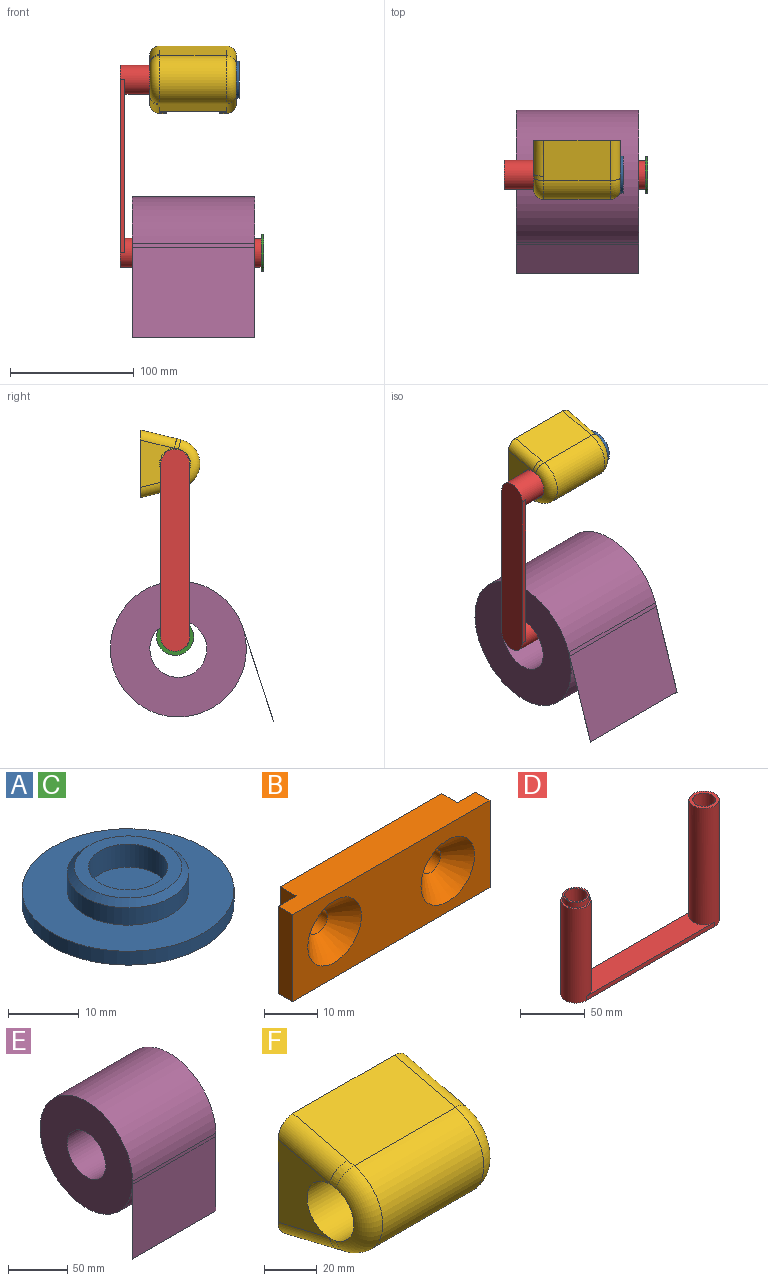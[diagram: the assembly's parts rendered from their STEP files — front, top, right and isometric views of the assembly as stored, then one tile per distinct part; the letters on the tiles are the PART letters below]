
ASSEMBLY  parts=6 mates=5
PART A: 8 faces, bbox 30x30x6.4 mm
  f0: cylinder r=15mm len=30mm, axis (0,0,-1), area 226.2mm2, adj f1,f2
  f1: plane 30x30mm, normal (0,0,1), area 474.5mm2, adj f0,f4
  f2: plane 30x30mm, normal (0,0,-1), area 706.9mm2, adj f0
  f3: cylinder r=5.6mm len=11.2mm, axis (0,0,-1), area 140.7mm2, adj f5,f6
  f4: cylinder r=8.6mm len=17.2mm, axis (0,0,-1), area 162.1mm2, adj f1,f7
  f5: plane 15.2x15.2mm, normal (0,0,1), area 82.9mm2, adj f3,f7
  f6: plane 11.2x11.2mm, normal (0,0,1), area 98.5mm2, adj f3
  f7: cone r=7.6mm half-angle=45deg, axis (0,0,-1), area 72mm2, adj f4,f5
PART B: 14 faces, bbox 52.4x8x20 mm
  f0: plane 42.8x20mm, normal (0,1,0), area 813.5mm2, adj f1,f7,f8,f9,f10,f11
  f1: plane 20x4.2mm, normal (-1,0,0), area 84mm2, adj f0,f2,f8,f9
  f2: plane 20x4.8mm, normal (0,1,0), area 96mm2, adj f1,f3,f8,f9
  f3: plane 20x3.8mm, normal (-1,0,0), area 76mm2, adj f2,f4,f8,f9
  f4: plane 52.4x20mm, normal (0,-1,0), area 731.3mm2, adj f3,f5,f8,f9,f12,f13
  f5: plane 20x3.8mm, normal (1,0,0), area 76mm2, adj f4,f6,f8,f9
  f6: plane 20x4.8mm, normal (0,1,0), area 96mm2, adj f5,f7,f8,f9
  f7: plane 20x4.2mm, normal (1,0,0), area 84mm2, adj f0,f6,f8,f9
  f8: plane 52.4x8mm, normal (0,0,1), area 378.9mm2, adj f0,f1,f2,f3,f4,f5,f6,f7
  f9: plane 52.4x8mm, normal (0,0,-1), area 378.9mm2, adj f0,f1,f2,f3,f4,f5,f6,f7
  f10: cylinder r=2.6mm len=5.2mm, axis (0,-1,0), area 57.2mm2, adj f0,f12
  f11: cylinder r=2.6mm len=5.2mm, axis (0,-1,0), area 57.2mm2, adj f0,f13
  f12: cone r=2.6mm half-angle=45deg, axis (0,-1,0), area 193.9mm2, adj f4,f10
  f13: cone r=2.6mm half-angle=45deg, axis (0,-1,0), area 193.9mm2, adj f4,f11
PART C: same geometry as A
PART D: 14 faces, bbox 163.4x23.4x114 mm
  f0: cylinder r=11.7mm len=88.9mm, axis (0,0,-1), area 6388.3mm2, adj f1,f3,f4,f5,f10
  f1: plane 140x4mm, normal (0,-1,0), area 560mm2, adj f0,f2,f4,f5
  f2: cylinder r=11.7mm len=114mm, axis (0,0,-1), area 8233.5mm2, adj f1,f3,f4,f5,f7
  f3: plane 140x4mm, normal (0,1,0), area 560mm2, adj f0,f2,f4,f5
  f4: plane 140x23.4mm, normal (0,0,1), area 2845.9mm2, adj f0,f1,f2,f3
  f5: plane 163.4x23.4mm, normal (0,0,-1), area 3706.1mm2, adj f0,f1,f2,f3
  f6: cylinder r=8.7mm len=110mm, axis (0,0,-1), area 6013mm2, adj f7,f8
  f7: plane 23.4x23.4mm, normal (0,0,1), area 192.3mm2, adj f2,f6
  f8: plane 17.4x17.4mm, normal (0,0,1), area 237.8mm2, adj f6
  f9: cylinder r=10.2mm len=20.4mm, axis (0,0,1), area 326.9mm2, adj f10,f13
  f10: plane 23.4x23.4mm, normal (0,0,1), area 103.2mm2, adj f0,f9
  f11: plane 17.4x17.4mm, normal (0,0,1), area 237.8mm2, adj f12
  f12: cylinder r=8.7mm len=90mm, axis (0,0,-1), area 4919.7mm2, adj f11,f13
  f13: plane 20.4x20.4mm, normal (0,0,1), area 89.1mm2, adj f9,f12
PART E: 7 faces, bbox 99x110x135 mm
  f0: cylinder r=55mm len=110mm, axis (-1,0,0), area 33883.5mm2, adj f2,f3,f4,f6
  f1: cylinder r=23mm len=99mm, axis (-1,0,0), area 14306.8mm2, adj f2,f3
  f2: plane 135x110mm, normal (1,0,0), area 7849.2mm2, adj f0,f1,f4,f5,f6
  f3: plane 135x110mm, normal (-1,0,0), area 7849.2mm2, adj f0,f1,f4,f5,f6
  f4: plane 99x76.69mm, normal (0,1,0), area 7591.8mm2, adj f0,f2,f3,f5
  f5: plane 99x0.1mm, normal (0,0,-1), area 9.9mm2, adj f2,f3,f4,f6
  f6: plane 99x80mm, normal (0,-1,0), area 7920mm2, adj f0,f2,f3,f5
PART F: 25 faces, bbox 70.4x51.5x54.6 mm
  f0: plane 54.02x32.67mm, normal (0,-0.23,-0.97), area 1408.5mm2, adj f3,f4,f12,f13,f16,f17,f18,f19
  f1: cylinder r=12.5mm len=65mm, axis (1,0,0), area 5105.1mm2, adj f6,f8,f10,f11,f13
  f2: plane 54.02x32.67mm, normal (0,-0.23,0.97), area 1814.3mm2, adj f3,f4,f9,f10,f14
  f3: cylinder r=20mm len=54.02mm, axis (-1,0,0), area 2884.8mm2, adj f0,f2,f11,f15
  f4: plane 70x54.58mm, normal (0,1,0), area 2216.2mm2, adj f0,f2,f5,f6,f9,f12,f14,f16
  f5: plane 40x38.13mm, normal (1,0,0), area 726mm2, adj f4,f7,f14,f15,f16
  f6: plane 38.13x27.4mm, normal (-1,0,0), area 634mm2, adj f1,f4,f9,f12
  f7: cylinder r=11mm len=22mm, axis (1,0,0), area 345.6mm2, adj f5,f8
  f8: plane 25x25mm, normal (-1,0,0), area 110.7mm2, adj f1,f7
  f9: cylinder r=8mm len=31.13mm, axis (0,-0.97,-0.23), area 369.4mm2, adj f2,f4,f6,f10
  f10: bspline ~8.53x8.36mm, area 42.8mm2, adj f1,f2,f9,f11
  f11: torus R=12mm, axis (-1,0,0), area 557.2mm2, adj f1,f3,f10,f13
  f12: cylinder r=8mm len=31.13mm, axis (0,0.97,-0.23), area 369.4mm2, adj f0,f4,f6,f13
  f13: bspline ~8.53x8.36mm, area 42.8mm2, adj f0,f1,f11,f12
  f14: cylinder r=8mm len=34.54mm, axis (0,0.97,0.23), area 413.4mm2, adj f2,f4,f5,f15
  f15: torus R=12mm, axis (1,0,0), area 573.6mm2, adj f3,f5,f14,f16
  f16: cylinder r=8mm len=34.54mm, axis (0,-0.97,0.23), area 413.4mm2, adj f0,f4,f5,f15
  f17: plane 35.04x5mm, normal (0,-1,0), area 175.2mm2, adj f0,f18,f23,f24
  f18: plane 36x4mm, normal (-1,0,0), area 142.1mm2, adj f0,f4,f17,f24
  f19: plane 36x4mm, normal (1,0,0), area 142.1mm2, adj f0,f4,f20,f24
  f20: plane 35.04x5mm, normal (0,-1,0), area 175.2mm2, adj f0,f19,f21,f24
  f21: plane 35.04x4.2mm, normal (1,0,0), area 145mm2, adj f0,f20,f22,f24
  f22: plane 53x34.03mm, normal (0,1,0), area 1803.7mm2, adj f0,f21,f23,f24
  f23: plane 35.04x4.2mm, normal (-1,0,0), area 145mm2, adj f0,f17,f22,f24
  f24: plane 53x8.2mm, normal (0,0,-1), area 394.6mm2, adj f4,f17,f18,f19,f20,f21,f22,f23
PLACE A rot(axis=(0.58,-0.58,-0.58),120deg) t=(37.4,-27.89,1.39)mm
PLACE B t=(0,0,-10)mm
PLACE C rot(axis=(0.58,-0.58,-0.58),120deg) t=(57.4,-27.89,-138.61)mm
PLACE D rot(axis=(0,1,0),90deg) t=(-59,-27.89,-68.61)mm
PLACE E rot(axis=(-1,0,0),18deg) t=(0.5,-30.49,-148.35)mm
PLACE F t=(0,0.11,-25.9)mm
MATE fastened D.f12 <-> A.f4  axis (1,0,0) through (35,-27.89,1.39)mm
MATE planar E.f2 <-> D.f6  axis (1,0,0) through (50,-30.56,-148.37)mm
MATE slider F.f24 <-> B.f8  axis (0,0,-1) through (0,-4.2,10.1)mm
MATE fastened D.f6 <-> C.f0  axis (-1,0,0) through (55,-27.89,-138.61)mm
MATE revolute D.f12 <-> F.f1  axis (1,0,0) through (35,-27.89,1.39)mm
